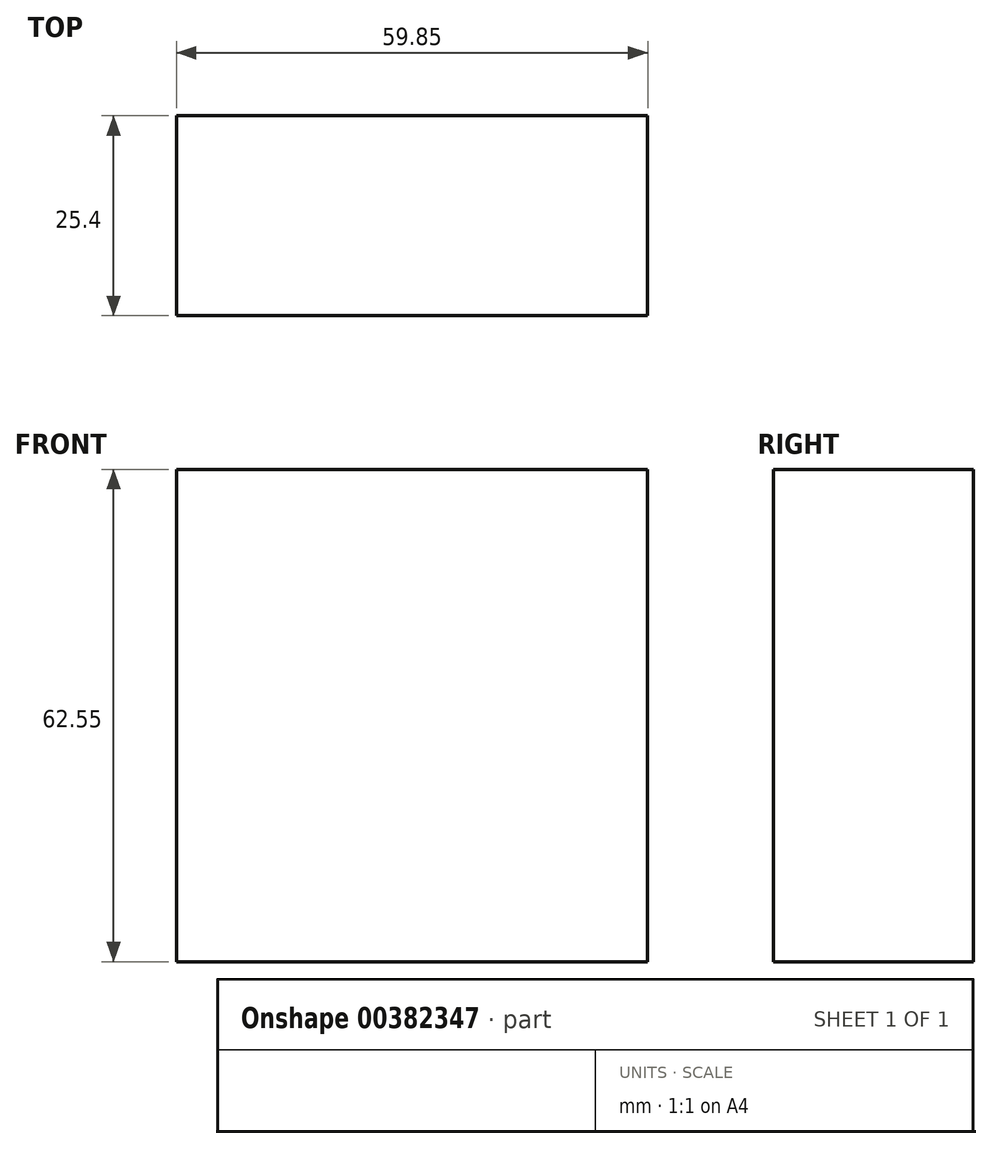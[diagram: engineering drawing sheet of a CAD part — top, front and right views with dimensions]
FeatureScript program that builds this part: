
annotation { "Feature Type Name" : "Feature", "Feature Type Description" : "" }
export const myFeature = defineFeature(function(context is Context, id is Id, definition is map)
    precondition{}
    {
        {
            var Q0;
            Q0=qCreatedBy(makeId("Front.planeOp"),FACE);
            var sketch = newSketch(context, id + "F0", { "sketchPlane" : qUnion([Q0])});
            skLineSegment(sketch, "E0.bottom", {"start": v(-37.07, 45.78) * mm, "end": v(22.78, 45.78) * mm});
            skLineSegment(sketch, "E0.top", {"start": v(-37.07, -16.77) * mm, "end": v(22.78, -16.77) * mm});
            skLineSegment(sketch, "E0.left", {"start": v(-37.07, 45.78) * mm, "end": v(-37.07, -16.77) * mm});
            skLineSegment(sketch, "E0.right", {"start": v(22.78, 45.78) * mm, "end": v(22.78, -16.77) * mm});
            skSolve(sketch);
        }
        {
            var Q0;
            Q0 = qSketchRegion(id + "F0", true);
            extrude(context, id + "F1", {"entities" : qUnion([Q0]), "depth" : 25.4 * mm});
        }
    });
